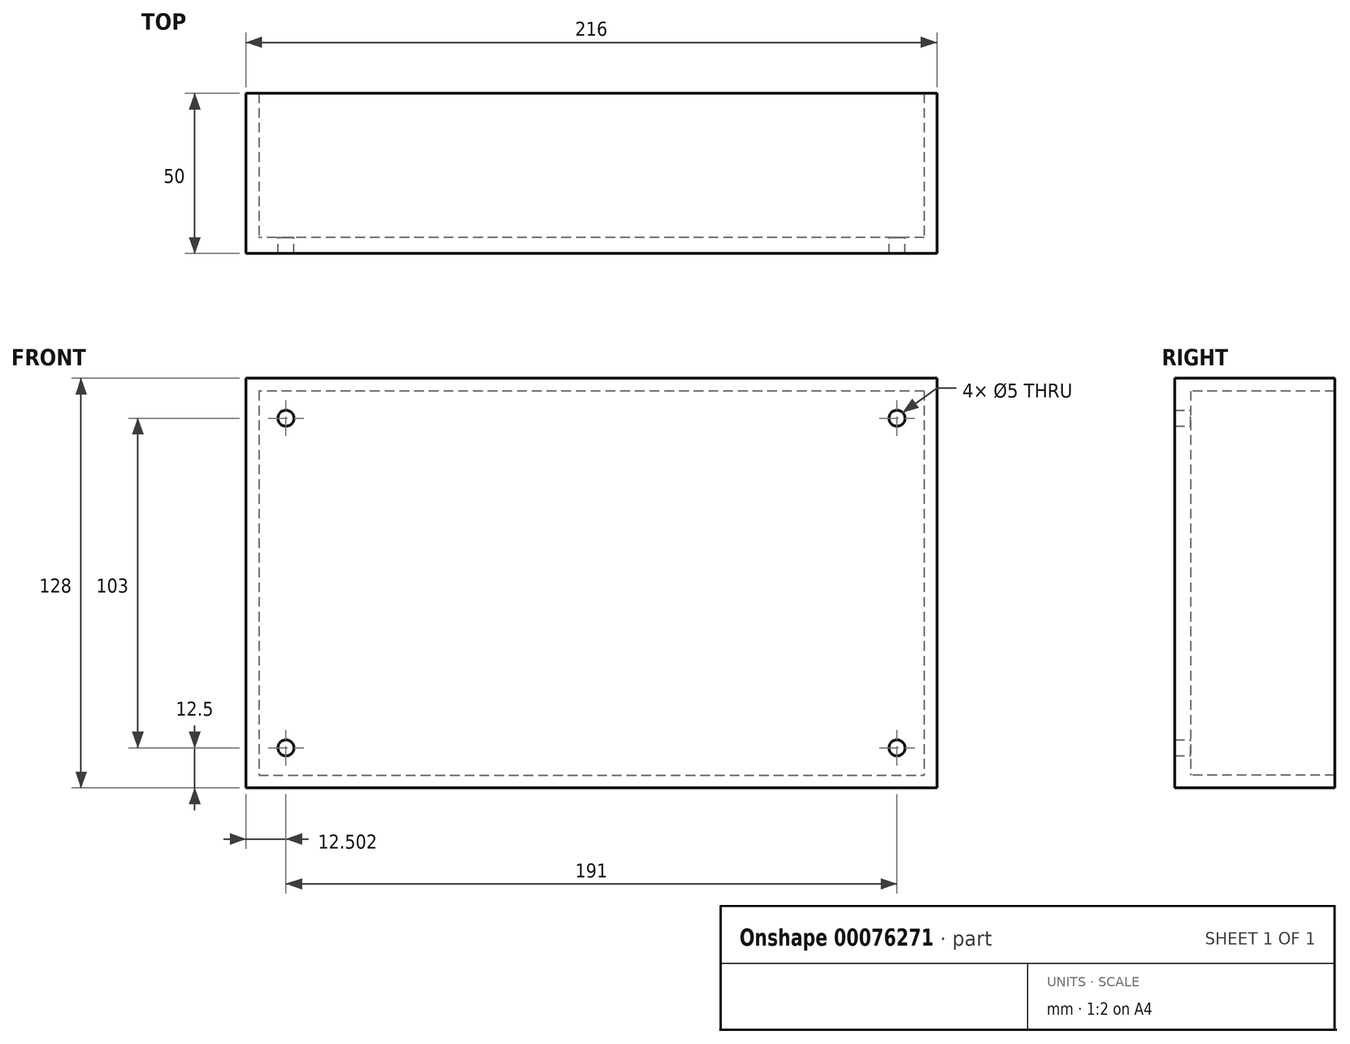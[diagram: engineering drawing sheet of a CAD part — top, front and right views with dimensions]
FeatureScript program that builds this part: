
annotation { "Feature Type Name" : "Feature", "Feature Type Description" : "" }
export const myFeature = defineFeature(function(context is Context, id is Id, definition is map)
    precondition{}
    {
        {
            var Q0;
            Q0=qCreatedBy(makeId("Front.planeOp"),FACE);
            var sketch = newSketch(context, id + "F0", { "sketchPlane" : qUnion([Q0])});
            skLineSegment(sketch, "E0.bottom", {"start": v(-115.73, -41.78) * mm, "end": v(100.27, -41.78) * mm});
            skLineSegment(sketch, "E0.top", {"start": v(-115.73, 86.22) * mm, "end": v(100.27, 86.22) * mm});
            skLineSegment(sketch, "E0.left", {"start": v(-115.73, -41.78) * mm, "end": v(-115.73, 86.22) * mm});
            skLineSegment(sketch, "E0.right", {"start": v(100.27, -41.78) * mm, "end": v(100.27, 86.22) * mm});
            skCircle(sketch, "E1", {"center": v(-103.23, 73.72) * mm, "radius": 2.5 * mm});
            skCircle(sketch, "E2", {"center": v(87.77, 73.72) * mm, "radius": 2.5 * mm});
            skCircle(sketch, "E3", {"center": v(87.77, -29.28) * mm, "radius": 2.5 * mm});
            skCircle(sketch, "E4", {"center": v(-103.23, -29.28) * mm, "radius": 2.5 * mm});
            skSolve(sketch);
        }
        {
            var Q0;
            Q0 = qSketchRegion(id + "F0", true);
            extrude(context, id + "F1", {"entities" : qUnion([Q0]), "depth" : 5 * mm});
        }
        {
            var Q0;
            Q0=makeQuery(id+"F1.opExtrude","CAP_FACE",FACE,{"disambiguationData":[OSD([sQuery(id+"F0.wireOp",EDGE,"E0.bottom"),sQuery(id+"F0.wireOp",EDGE,"E0.top"),sQuery(id+"F0.wireOp",EDGE,"E0.left"),sQuery(id+"F0.wireOp",EDGE,"E0.right"),sQuery(id+"F0.wireOp",EDGE,"E1"),sQuery(id+"F0.wireOp",EDGE,"E2"),sQuery(id+"F0.wireOp",EDGE,"E3"),sQuery(id+"F0.wireOp",EDGE,"E4")])],"isStart":true});
            var sketch = newSketch(context, id + "F2", { "sketchPlane" : qUnion([Q0])});
            skLineSegment(sketch, "E5", {"start": v(-100.27, 86.22) * mm, "end": v(-100.27, -41.78) * mm});
            skLineSegment(sketch, "E6", {"start": v(-100.27, -41.78) * mm, "end": v(115.73, -41.78) * mm});
            skLineSegment(sketch, "E7", {"start": v(115.73, -41.78) * mm, "end": v(115.73, 86.22) * mm});
            skLineSegment(sketch, "E8", {"start": v(115.73, 86.22) * mm, "end": v(-100.27, 86.22) * mm});
            skLineSegment(sketch, "E9", {"start": v(-96.27, 82.22) * mm, "end": v(-96.27, -37.78) * mm});
            skLineSegment(sketch, "E10", {"start": v(-96.27, 82.22) * mm, "end": v(111.73, 82.22) * mm});
            skLineSegment(sketch, "E11", {"start": v(111.73, 82.22) * mm, "end": v(111.73, -37.78) * mm});
            skLineSegment(sketch, "E12", {"start": v(111.73, -37.78) * mm, "end": v(-96.27, -37.78) * mm});
            skSolve(sketch);
        }
        {
            var Q0;
            Q0 = qSketchRegion(id + "F2", true);
            extrude(context, id + "F3", {"entities" : qUnion([Q0]), "operationType" : NewBodyOperationType.ADD, "depth" : 45 * mm, "offsetDistance" : 25 * mm});
        }
    });
